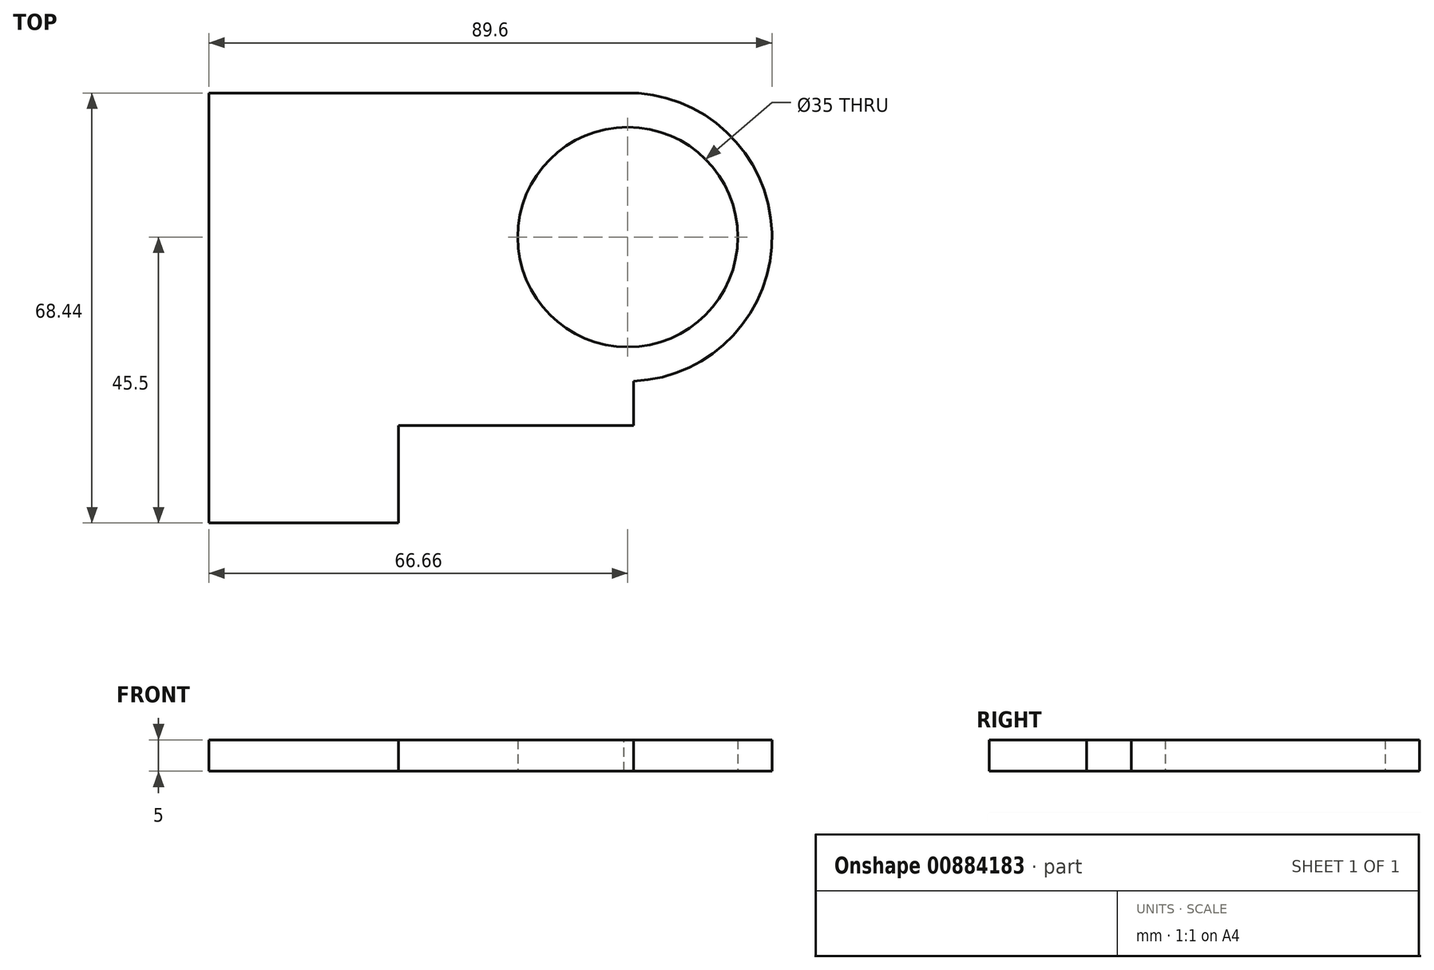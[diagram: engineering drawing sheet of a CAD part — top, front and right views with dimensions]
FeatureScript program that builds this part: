
annotation { "Feature Type Name" : "Feature", "Feature Type Description" : "" }
export const myFeature = defineFeature(function(context is Context, id is Id, definition is map)
    precondition{}
    {
        {
            var Q0;
            Q0=qCreatedBy(makeId("Top.planeOp"),FACE);
            var sketch = newSketch(context, id + "F0", { "sketchPlane" : qUnion([Q0])});
            skLineSegment(sketch, "E0.bottom", {"start": v(0, 0) * mm, "end": v(60, 0) * mm});
            skLineSegment(sketch, "E0.top", {"start": v(5, 55.23) * mm, "end": v(55, 55.23) * mm});
            skLineSegment(sketch, "E0.left", {"start": v(0, 0) * mm, "end": v(0, 50.23) * mm});
            skLineSegment(sketch, "E0.right", {"start": v(60, 0) * mm, "end": v(60, 50.23) * mm});
            skLineSegment(sketch, "E1", {"start": v(30, 0) * mm, "end": v(30, 55.23) * mm, "construction": true});
            skCircle(sketch, "E2", {"center": v(30, 30) * mm, "radius": 17.5 * mm});
            skPoint(sketch, "E3.visualSharp", {"position": v(0, 55.23) * mm});
            skArc(sketch, "E3.filletArc", {"start": v(5, 55.23) * mm, "mid": v(1.46, 53.77) * mm, "end": v(0, 50.23) * mm});
            skPoint(sketch, "E4.visualSharp", {"position": v(60, 55.23) * mm});
            skArc(sketch, "E4.filletArc", {"start": v(60, 50.23) * mm, "mid": v(58.54, 53.77) * mm, "end": v(55, 55.23) * mm});
            skSolve(sketch);
        }
        {
            var Q0;
            Q0=qSketchRegion(id+"F0",true);
            extrude(context, id + "F1", {"entities" : qUnion([Q0]), "depth" : 5 * mm, "offsetDistance" : 25 * mm});
        }
        {
            var Q0;
            Q0=makeQuery(id+"F1.opExtrude","CAP_FACE",FACE,{"disambiguationData":[OSD([sQuery(id+"F0.wireOp",EDGE,"E0.bottom"),sQuery(id+"F0.wireOp",EDGE,"E0.top"),sQuery(id+"F0.wireOp",EDGE,"E0.left"),sQuery(id+"F0.wireOp",EDGE,"E0.right"),sQuery(id+"F0.wireOp",EDGE,"E2"),sQuery(id+"F0.wireOp",EDGE,"E3.filletArc"),sQuery(id+"F0.wireOp",EDGE,"E4.filletArc")])],"isStart":false});
            var sketch = newSketch(context, id + "F2", { "sketchPlane" : qUnion([Q0])});
            skLineSegment(sketch, "E5", {"start": v(0, 36.83) * mm, "end": v(-6.45, 36.83) * mm});
            skLineSegment(sketch, "E6", {"start": v(-6.45, 36.83) * mm, "end": v(-6.45, -38.62) * mm});
            skLineSegment(sketch, "E7", {"start": v(-6.45, -38.62) * mm, "end": v(0, -38.62) * mm});
            skLineSegment(sketch, "E8", {"start": v(0, -38.62) * mm, "end": v(0, 0) * mm});
            skLineSegment(sketch, "E9", {"start": v(-6.45, -38.62) * mm, "end": v(-36.66, -38.62) * mm});
            skLineSegment(sketch, "E10", {"start": v(-36.66, -38.62) * mm, "end": v(-36.66, 55.23) * mm});
            skLineSegment(sketch, "E11", {"start": v(-36.66, 55.23) * mm, "end": v(5.84, 55.23) * mm});
            skLineSegment(sketch, "E12", {"start": v(0, 0) * mm, "end": v(-6.45, 0) * mm});
            skSolve(sketch);
        }
        {
            var Q0;
            {var subQ1=sQuery(id+"F2.wireOp",EDGE,"E5");Q0=makeQuery(id+"F2.imprint","IMPRINT",FACE,{"disambiguationData":[TD([[makeQuery(id+"F2.imprint","IMPRINT",EDGE,{"derivedFrom":subQ1}),1.0]])]});}
            var Q1;
            {var subQ4=sQuery(id+"F2.wireOp",EDGE,"E5");Q1=makeQuery(id+"F2.imprint","IMPRINT",FACE,{"disambiguationData":[TD([[makeQuery(id+"F2.imprint","IMPRINT",EDGE,{"derivedFrom":subQ4}),-1.0]])]});}
            extrude(context, id + "F3", {"entities" : qUnion([Q0, Q1]), "operationType" : NewBodyOperationType.ADD, "oppositeDirection" : true, "depth" : 5 * mm, "offsetDistance" : 25 * mm});
        }
        {
            var Q0;
            {var subQ0=sQuery(id+"F0.wireOp",EDGE,"E0.left");Q0=makeQuery(id+"F3.boolean.opBoolean","MERGE",FACE,{"derivedFrom":[makeQuery(id+"F1.opExtrude","CAP_FACE",FACE,{"disambiguationData":[OSD([sQuery(id+"F0.wireOp",EDGE,"E0.bottom"),sQuery(id+"F0.wireOp",EDGE,"E0.top"),subQ0,sQuery(id+"F0.wireOp",EDGE,"E0.right"),sQuery(id+"F0.wireOp",EDGE,"E2"),sQuery(id+"F0.wireOp",EDGE,"E3.filletArc"),sQuery(id+"F0.wireOp",EDGE,"E4.filletArc")])],"isStart":false}),makeQuery(id+"F3.opExtrude","CAP_FACE",FACE,{"disambiguationData":[OSD([subQ0,sQuery(id+"F2.wireOp",EDGE,"E5"),sQuery(id+"F2.wireOp",EDGE,"E6"),sQuery(id+"F2.wireOp",EDGE,"E7"),sQuery(id+"F2.wireOp",EDGE,"E8")])],"isStart":true})]});}
            var sketch = newSketch(context, id + "F4", { "sketchPlane" : qUnion([Q0])});
            skLineSegment(sketch, "E13", {"start": v(49.35, 0) * mm, "end": v(66.44, 0) * mm});
            skLineSegment(sketch, "E14", {"start": v(66.44, 0) * mm, "end": v(66.44, 55.23) * mm});
            skLineSegment(sketch, "E15", {"start": v(66.44, 55.23) * mm, "end": v(49.35, 55.23) * mm});
            skLineSegment(sketch, "E16", {"start": v(54.2, 0) * mm, "end": v(54.2, 55.23) * mm});
            skLineSegment(sketch, "E17", {"start": v(54.2, 55.23) * mm, "end": v(49.35, 55.23) * mm});
            skSolve(sketch);
        }
        {
            var Q0;
            Q0 = qSketchRegion(id + "F4", true);
            extrude(context, id + "F5", {"entities" : qUnion([Q0]), "operationType" : NewBodyOperationType.REMOVE, "oppositeDirection" : true, "depth" : 25 * mm, "offsetDistance" : 25 * mm});
        }
        {
            var Q0;
            {var subQ0=sQuery(id+"F0.wireOp",EDGE,"E3.filletArc");var subQ1=sQuery(id+"F0.wireOp",EDGE,"E0.left");Q0=makeQuery(id+"F3.boolean.opBoolean","MERGE",FACE,{"derivedFrom":[makeQuery(id+"F1.opExtrude","CAP_FACE",FACE,{"disambiguationData":[OSD([sQuery(id+"F0.wireOp",EDGE,"E0.bottom"),sQuery(id+"F0.wireOp",EDGE,"E0.top"),subQ1,sQuery(id+"F0.wireOp",EDGE,"E0.right"),sQuery(id+"F0.wireOp",EDGE,"E2"),subQ0,sQuery(id+"F0.wireOp",EDGE,"E4.filletArc")])],"isStart":false}),makeQuery(id+"F3.opExtrude","CAP_FACE",FACE,{"disambiguationData":[OSD([subQ1,subQ0,sQuery(id+"F2.wireOp",EDGE,"E6"),sQuery(id+"F2.wireOp",EDGE,"E9"),sQuery(id+"F2.wireOp",EDGE,"E10"),sQuery(id+"F2.wireOp",EDGE,"E11"),sQuery(id+"F2.wireOp",EDGE,"E12")])],"isStart":true})]});}
            var sketch = newSketch(context, id + "F6", { "sketchPlane" : qUnion([Q0])});
            skCircle(sketch, "E18", {"center": v(30, 30) * mm, "radius": 22.94 * mm});
            skLineSegment(sketch, "E19", {"start": v(29.4, 52.94) * mm, "end": v(-36.66, 52.94) * mm});
            skLineSegment(sketch, "E20", {"start": v(30.91, 7.07) * mm, "end": v(30.91, 0) * mm});
            skLineSegment(sketch, "E21", {"start": v(30.91, 0) * mm, "end": v(-36.66, 0) * mm});
            skLineSegment(sketch, "E22", {"start": v(-36.66, 0) * mm, "end": v(-36.66, 52.94) * mm});
            skSolve(sketch);
        }
        {
            var Q0;
            {var subQ4=sQuery(id+"F6.wireOp",EDGE,"E19");Q0=makeQuery(id+"F6.imprint","IMPRINT",FACE,{"disambiguationData":[TD([[makeQuery(id+"F6.imprint","IMPRINT",EDGE,{"derivedFrom":subQ4}),-1.0]])]});}
            extrude(context, id + "F7", {"entities" : qUnion([Q0]), "operationType" : NewBodyOperationType.REMOVE, "oppositeDirection" : true, "depth" : 25 * mm, "offsetDistance" : 25 * mm});
        }
        {
            var Q0;
            {var subQ0=sQuery(id+"F0.wireOp",EDGE,"E3.filletArc");var subQ1=sQuery(id+"F0.wireOp",EDGE,"E0.left");Q0=makeQuery(id+"F3.boolean.opBoolean","MERGE",FACE,{"derivedFrom":[makeQuery(id+"F1.opExtrude","CAP_FACE",FACE,{"disambiguationData":[OSD([sQuery(id+"F0.wireOp",EDGE,"E0.bottom"),sQuery(id+"F0.wireOp",EDGE,"E0.top"),subQ1,sQuery(id+"F0.wireOp",EDGE,"E0.right"),sQuery(id+"F0.wireOp",EDGE,"E2"),subQ0,sQuery(id+"F0.wireOp",EDGE,"E4.filletArc")])],"isStart":false}),makeQuery(id+"F3.opExtrude","CAP_FACE",FACE,{"disambiguationData":[OSD([subQ1,subQ0,sQuery(id+"F2.wireOp",EDGE,"E6"),sQuery(id+"F2.wireOp",EDGE,"E9"),sQuery(id+"F2.wireOp",EDGE,"E10"),sQuery(id+"F2.wireOp",EDGE,"E11"),sQuery(id+"F2.wireOp",EDGE,"E12")])],"isStart":true})]});}
            var sketch = newSketch(context, id + "F8", { "sketchPlane" : qUnion([Q0])});
            skLineSegment(sketch, "E23", {"start": v(-6.45, 0) * mm, "end": v(-6.45, -15.5) * mm});
            skLineSegment(sketch, "E24", {"start": v(-6.45, -15.5) * mm, "end": v(-36.66, -15.5) * mm});
            skLineSegment(sketch, "E25", {"start": v(-36.66, -15.5) * mm, "end": v(-36.66, -38.62) * mm});
            skLineSegment(sketch, "E26", {"start": v(-36.66, -38.62) * mm, "end": v(-6.45, -38.62) * mm});
            skLineSegment(sketch, "E27", {"start": v(-6.45, -38.62) * mm, "end": v(-6.45, -15.5) * mm});
            skSolve(sketch);
        }
        {
            var Q0;
            Q0 = qSketchRegion(id + "F8", true);
            extrude(context, id + "F9", {"entities" : qUnion([Q0]), "operationType" : NewBodyOperationType.REMOVE, "oppositeDirection" : true, "depth" : 25 * mm, "offsetDistance" : 25 * mm});
        }
    });
